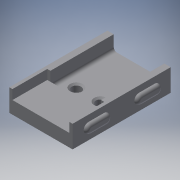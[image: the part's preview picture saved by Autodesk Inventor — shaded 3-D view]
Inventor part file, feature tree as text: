
AUTODESK INVENTOR PART (.ipt)
format: ipt  version: 2018 (Build 220112000, 112)  size: 222,720 bytes
history: native  units: mm
features: extrude x5, sketch x5, chamfer x2, fillet x2, plane x1, mirror x1, projected_geometry x1
ambient origin geometry x8: Origin, YZ Plane, XZ Plane, XY Plane, X Axis, Y Axis, Z Axis, Center Point
bodies: Solid1 (feature_tree)
feature tree (17):
  extrude  "Extrusion1"  Depth=31.0mm
  extrude  "Extrusion2"  Depth=20.0mm
  extrude  "Extrusion3"  Depth=2.0mm
  extrude  "Extrusion4"  Depth=1.0mm
  chamfer  "Chamfer1"  Distance=3.0mm
  extrude  "Extrusion5"  Depth=3.0mm
  plane  "Work Plane1"
  mirror  "Mirror1"
  fillet  "Fillet2"  Radius=3.0mm
  fillet  "Fillet3"  Radius=7.62mm
  chamfer  "Chamfer2"  Distance=15.0mm
  sketch  "Sketch1"  dims[d0=20.0mm d1=31.0mm]
  sketch  "Sketch2"  dims[d2=7.0mm d3=0.0mm d4=20.0mm]
  sketch  "Sketch3"  dims[d5=2.0mm d6=2.0mm]
  sketch  "Sketch4"  dims[d7=4.5mm d8=0.0mm d9=1.0mm]
  projected_geometry  "Projected Loop1"
  sketch  "Sketch5"  dims[d10=1.0mm d11=3.0mm d12=0.0mm d13=3.0mm d14=3.0mm d15=7.62mm d16=15.0mm d17=90.0deg d18=3.0mm d19=0.0mm d20=0.5mm d21=2.0mm d22=45.0deg d23=31.0mm d24=90.0deg d25=3.0mm d26=3.0mm d27=5.0mm d28=5.0mm d29=5.0mm d30=5.0mm d31=1.0mm d32=0.0mm d34=1.0mm d35=1.0mm d36=0.5mm d37=2.0mm d38=45.0deg]
